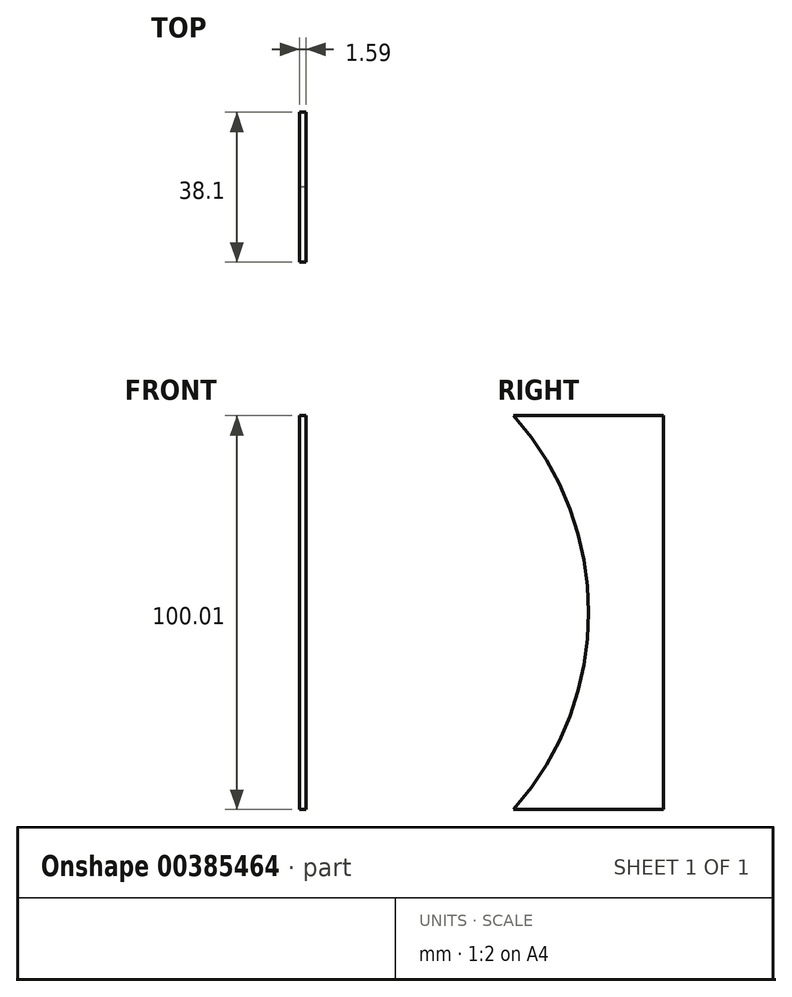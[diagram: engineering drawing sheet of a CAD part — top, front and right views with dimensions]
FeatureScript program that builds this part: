
annotation { "Feature Type Name" : "Feature", "Feature Type Description" : "" }
export const myFeature = defineFeature(function(context is Context, id is Id, definition is map)
    precondition{}
    {
        {
            var Q0;
            Q0=qCreatedBy(makeId("Right.planeOp"),FACE);
            var sketch = newSketch(context, id + "F0", { "sketchPlane" : qUnion([Q0])});
            skLineSegment(sketch, "E0.bottom", {"start": v(0, 0) * mm, "end": v(-38.1, 0) * mm});
            skLineSegment(sketch, "E0.left", {"start": v(0, 0) * mm, "end": v(0, 100.01) * mm});
            skLineSegment(sketch, "E1", {"start": v(0, 100.01) * mm, "end": v(-38.1, 100.01) * mm});
            skArc(sketch, "E2", {"start": v(-38.1, 0) * mm, "mid": v(-19.05, 50) * mm, "end": v(-38.1, 100.01) * mm});
            skSolve(sketch);
        }
        {
            var Q0;
            Q0 = qSketchRegion(id + "F0", true);
            extrude(context, id + "F1", {"entities" : qUnion([Q0]), "depth" : 1.59 * mm});
        }
    });
